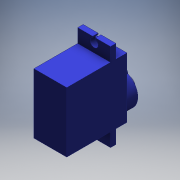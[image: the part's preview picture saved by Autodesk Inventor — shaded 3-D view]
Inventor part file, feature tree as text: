
AUTODESK INVENTOR PART (.ipt)
format: ipt  version: 2016 (Build 200138000, 138)  size: 165,888 bytes
history: native  units: mm
features: extrude x5, sketch x5, other x1, mirror x1
ambient origin geometry x8: Origin, YZ Plane, XZ Plane, XY Plane, X Axis, Y Axis, Z Axis, Center Point
bodies: Body1 (feature_tree)
feature tree (12):
  other  "Sólido1"
  extrude  "Extrusión1"  Depth=5.0mm TaperAngle=0.0deg
  extrude  "Extrusión2"  Depth=4.0mm TaperAngle=0.0deg
  extrude  "Extrusión3"  [1 undecoded]
  mirror  "Simetría1"
  extrude  "Extrusión4"  [1 undecoded]
  extrude  "Extrusión5"  [1 undecoded]
  sketch  "Boceto1"  dims[d2=22.0mm d3=0.0mm d6=5.0mm d7=0.0mm]
  sketch  "Boceto2"  dims[d12=5.0mm d13=0.0mm d19=4.0mm d20=0.0mm]
  sketch  "Boceto3"  dims[d23=3.0mm d24=0.0mm]
  sketch  "Boceto5"
  sketch  "Boceto6"
note: 3 required parameter values undecoded (feature->parameter linkage not recoverable at this tier; creation-order binding heuristic only, values carry confidence <= 0.55)
